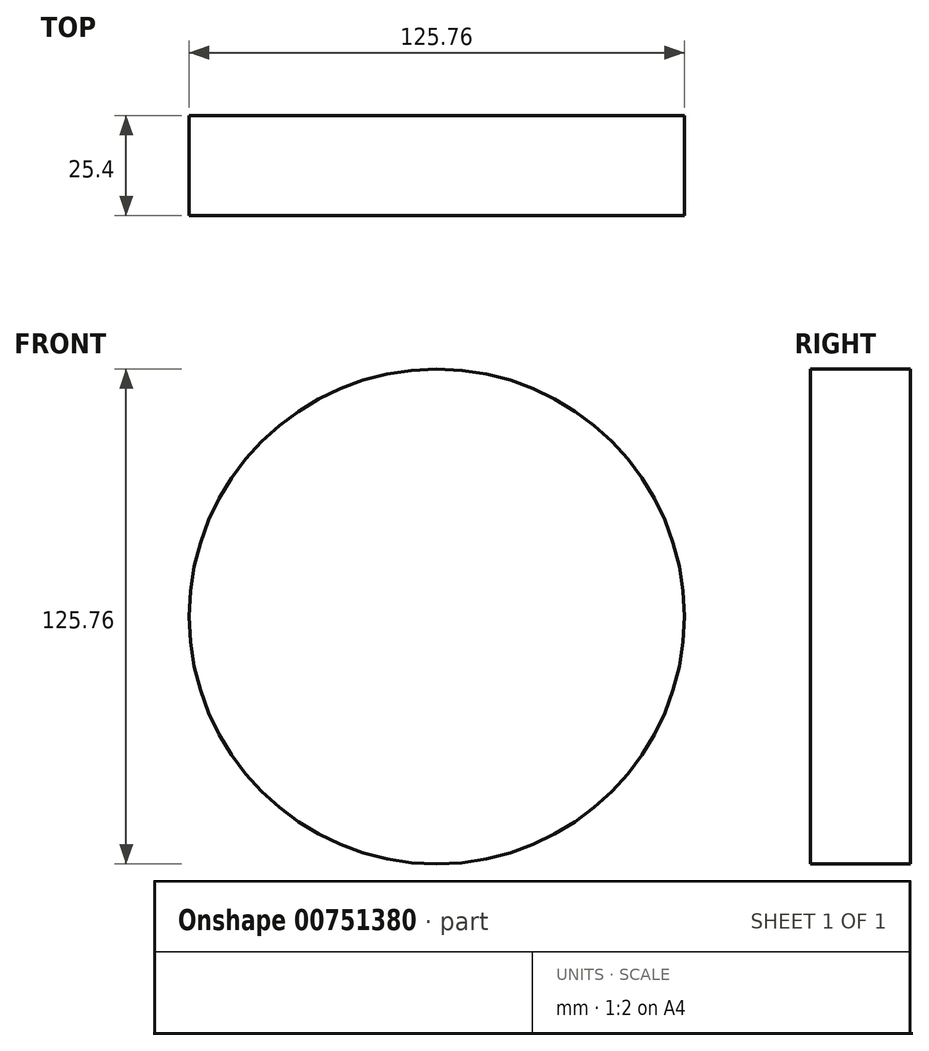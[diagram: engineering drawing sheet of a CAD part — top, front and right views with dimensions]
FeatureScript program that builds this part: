
annotation { "Feature Type Name" : "Feature", "Feature Type Description" : "" }
export const myFeature = defineFeature(function(context is Context, id is Id, definition is map)
    precondition{}
    {
        {
            var Q0;
            Q0=qCreatedBy(makeId("Front.planeOp"),FACE);
            var sketch = newSketch(context, id + "F0", { "sketchPlane" : qUnion([Q0])});
            skCircle(sketch, "E0", {"center": v(0, 0) * mm, "radius": 62.88 * mm});
            skSolve(sketch);
        }
        {
            var Q0;
            Q0 = qSketchRegion(id + "F0", true);
            extrude(context, id + "F1", {"entities" : qUnion([Q0]), "depth" : 25.4 * mm, "offsetDistance" : 25.4 * mm});
        }
    });
